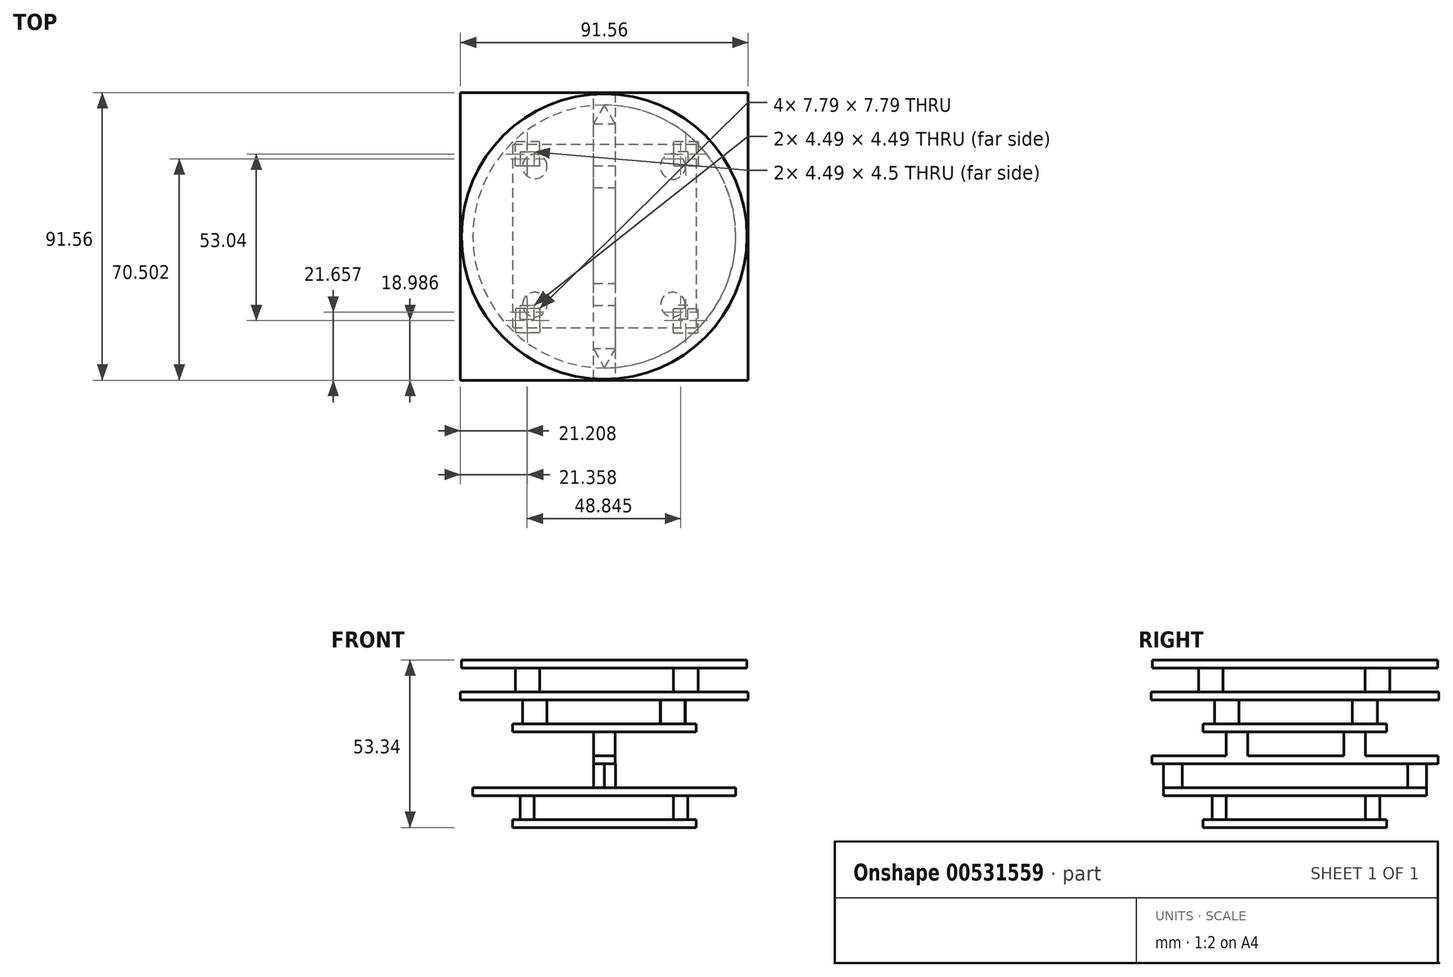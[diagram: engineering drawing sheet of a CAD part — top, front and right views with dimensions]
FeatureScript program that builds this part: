
annotation { "Feature Type Name" : "Feature", "Feature Type Description" : "" }
export const myFeature = defineFeature(function(context is Context, id is Id, definition is map)
    precondition{}
    {
        {
            var Q0;
            Q0=qCreatedBy(makeId("Top.planeOp"),FACE);
            var sketch = newSketch(context, id + "F0", { "sketchPlane" : qUnion([Q0])});
            skLineSegment(sketch, "E0.bottom", {"start": v(29.2, 29.21) * mm, "end": v(-29.21, 29.21) * mm});
            skLineSegment(sketch, "E0.top", {"start": v(29.21, -29.21) * mm, "end": v(-29.2, -29.21) * mm});
            skLineSegment(sketch, "E0.left", {"start": v(29.2, 29.21) * mm, "end": v(29.21, -29.21) * mm});
            skLineSegment(sketch, "E0.right", {"start": v(-29.21, 29.21) * mm, "end": v(-29.2, -29.21) * mm});
            skPoint(sketch, "E0.middle", {"position": v(0, 0) * mm});
            skSolve(sketch);
        }
        {
            var Q0;
            Q0 = qSketchRegion(id + "F0", true);
            extrude(context, id + "F1", {"entities" : qUnion([Q0]), "depth" : 2.54 * mm, "offsetDistance" : 25.4 * mm});
        }
        {
            var Q0;
            Q0=makeQuery(id+"F1.opExtrude","CAP_FACE",FACE,{"disambiguationData":[OSD([sQuery(id+"F0.wireOp",EDGE,"E0.bottom"),sQuery(id+"F0.wireOp",EDGE,"E0.top"),sQuery(id+"F0.wireOp",EDGE,"E0.left"),sQuery(id+"F0.wireOp",EDGE,"E0.right")])],"isStart":false});
            var sketch = newSketch(context, id + "F2", { "sketchPlane" : qUnion([Q0])});
            skLineSegment(sketch, "E1.bottom", {"start": v(-26.82, 26.97) * mm, "end": v(-22.32, 26.97) * mm});
            skLineSegment(sketch, "E1.top", {"start": v(-26.82, 22.47) * mm, "end": v(-22.32, 22.47) * mm});
            skLineSegment(sketch, "E1.left", {"start": v(-26.82, 26.97) * mm, "end": v(-26.82, 22.47) * mm});
            skLineSegment(sketch, "E1.right", {"start": v(-22.32, 26.97) * mm, "end": v(-22.32, 22.47) * mm});
            skSolve(sketch);
        }
        {
            var Q0;
            Q0 = qSketchRegion(id + "F2", true);
            extrude(context, id + "F3", {"entities" : qUnion([Q0]), "operationType" : NewBodyOperationType.ADD, "depth" : 7.62 * mm, "offsetDistance" : 25.4 * mm});
        }
        {
            var Q0;
            Q0=makeQuery(id+"F1.opExtrude","CAP_FACE",FACE,{"disambiguationData":[OSD([sQuery(id+"F0.wireOp",EDGE,"E0.bottom"),sQuery(id+"F0.wireOp",EDGE,"E0.top"),sQuery(id+"F0.wireOp",EDGE,"E0.left"),sQuery(id+"F0.wireOp",EDGE,"E0.right")])],"isStart":false});
            var sketch = newSketch(context, id + "F4", { "sketchPlane" : qUnion([Q0])});
            skLineSegment(sketch, "E2.bottom", {"start": v(26.52, 26.97) * mm, "end": v(22.03, 26.97) * mm});
            skLineSegment(sketch, "E2.top", {"start": v(26.52, 22.47) * mm, "end": v(22.03, 22.47) * mm});
            skLineSegment(sketch, "E2.left", {"start": v(26.52, 26.97) * mm, "end": v(26.52, 22.47) * mm});
            skLineSegment(sketch, "E2.right", {"start": v(22.03, 26.97) * mm, "end": v(22.03, 22.47) * mm});
            skSolve(sketch);
        }
        {
            var Q0;
            Q0 = qSketchRegion(id + "F4", true);
            extrude(context, id + "F5", {"entities" : qUnion([Q0]), "operationType" : NewBodyOperationType.ADD, "depth" : 7.62 * mm, "offsetDistance" : 25.4 * mm});
        }
        {
            var Q0;
            Q0=makeQuery(id+"F1.opExtrude","CAP_FACE",FACE,{"disambiguationData":[OSD([sQuery(id+"F0.wireOp",EDGE,"E0.bottom"),sQuery(id+"F0.wireOp",EDGE,"E0.top"),sQuery(id+"F0.wireOp",EDGE,"E0.left"),sQuery(id+"F0.wireOp",EDGE,"E0.right")])],"isStart":false});
            var sketch = newSketch(context, id + "F6", { "sketchPlane" : qUnion([Q0])});
            skLineSegment(sketch, "E3.bottom", {"start": v(-26.82, -26.37) * mm, "end": v(-22.32, -26.37) * mm});
            skLineSegment(sketch, "E3.top", {"start": v(-26.82, -21.88) * mm, "end": v(-22.32, -21.88) * mm});
            skLineSegment(sketch, "E3.left", {"start": v(-26.82, -26.37) * mm, "end": v(-26.82, -21.88) * mm});
            skLineSegment(sketch, "E3.right", {"start": v(-22.32, -26.37) * mm, "end": v(-22.32, -21.88) * mm});
            skSolve(sketch);
        }
        {
            var Q0;
            Q0 = qSketchRegion(id + "F6", true);
            extrude(context, id + "F7", {"entities" : qUnion([Q0]), "operationType" : NewBodyOperationType.ADD, "depth" : 7.62 * mm, "offsetDistance" : 25.4 * mm});
        }
        {
            var Q0;
            Q0=makeQuery(id+"F1.opExtrude","CAP_FACE",FACE,{"disambiguationData":[OSD([sQuery(id+"F0.wireOp",EDGE,"E0.bottom"),sQuery(id+"F0.wireOp",EDGE,"E0.top"),sQuery(id+"F0.wireOp",EDGE,"E0.left"),sQuery(id+"F0.wireOp",EDGE,"E0.right")])],"isStart":false});
            var sketch = newSketch(context, id + "F8", { "sketchPlane" : qUnion([Q0])});
            skLineSegment(sketch, "E4.bottom", {"start": v(26.52, -26.37) * mm, "end": v(22.03, -26.37) * mm});
            skLineSegment(sketch, "E4.top", {"start": v(26.52, -21.88) * mm, "end": v(22.03, -21.88) * mm});
            skLineSegment(sketch, "E4.left", {"start": v(26.52, -26.37) * mm, "end": v(26.52, -21.88) * mm});
            skLineSegment(sketch, "E4.right", {"start": v(22.03, -26.37) * mm, "end": v(22.03, -21.88) * mm});
            skSolve(sketch);
        }
        {
            var Q0;
            Q0 = qSketchRegion(id + "F8", true);
            extrude(context, id + "F9", {"entities" : qUnion([Q0]), "operationType" : NewBodyOperationType.ADD, "depth" : 7.62 * mm, "offsetDistance" : 25.4 * mm});
        }
        {
            var Q0;
            Q0=makeQuery(id+"F3.opExtrude","CAP_FACE",FACE,{"disambiguationData":[OSD([sQuery(id+"F2.wireOp",EDGE,"E1.bottom"),sQuery(id+"F2.wireOp",EDGE,"E1.top"),sQuery(id+"F2.wireOp",EDGE,"E1.left"),sQuery(id+"F2.wireOp",EDGE,"E1.right")])],"isStart":false});
            var sketch = newSketch(context, id + "F10", { "sketchPlane" : qUnion([Q0])});
            skCircle(sketch, "E5", {"center": v(0, 0) * mm, "radius": 41.85 * mm});
            skSolve(sketch);
        }
        {
            var Q0;
            Q0 = qSketchRegion(id + "F10", true);
            extrude(context, id + "F11", {"entities" : qUnion([Q0]), "operationType" : NewBodyOperationType.ADD, "depth" : 2.54 * mm, "offsetDistance" : 25.4 * mm});
        }
        {
            var Q0;
            Q0=makeQuery(id+"F11.opExtrude","CAP_FACE",FACE,{"disambiguationData":[OSD([sQuery(id+"F10.wireOp",EDGE,"E5")])],"isStart":false});
            var sketch = newSketch(context, id + "F12", { "sketchPlane" : qUnion([Q0])});
            skLineSegment(sketch, "E6", {"start": v(0, 41.85) * mm, "end": v(-3.46, 35.87) * mm});
            skLineSegment(sketch, "E7", {"start": v(-3.46, 35.87) * mm, "end": v(3.45, 35.87) * mm});
            skLineSegment(sketch, "E8", {"start": v(3.45, 35.87) * mm, "end": v(0, 41.85) * mm});
            skSolve(sketch);
        }
        {
            var Q0;
            Q0 = qSketchRegion(id + "F12", true);
            extrude(context, id + "F13", {"entities" : qUnion([Q0]), "operationType" : NewBodyOperationType.ADD, "depth" : 7.62 * mm, "offsetDistance" : 25.4 * mm});
        }
        {
            var Q0;
            Q0=makeQuery(id+"F11.opExtrude","CAP_FACE",FACE,{"disambiguationData":[OSD([sQuery(id+"F10.wireOp",EDGE,"E5")])],"isStart":false});
            var sketch = newSketch(context, id + "F14", { "sketchPlane" : qUnion([Q0])});
            skLineSegment(sketch, "E9", {"start": v(0, -41.85) * mm, "end": v(3.53, -35.83) * mm});
            skLineSegment(sketch, "E10", {"start": v(3.53, -35.83) * mm, "end": v(-3.38, -35.83) * mm});
            skLineSegment(sketch, "E11", {"start": v(-3.38, -35.83) * mm, "end": v(0, -41.85) * mm});
            skSolve(sketch);
        }
        {
            var Q0;
            Q0 = qSketchRegion(id + "F14", true);
            extrude(context, id + "F15", {"entities" : qUnion([Q0]), "operationType" : NewBodyOperationType.ADD, "depth" : 7.62 * mm, "offsetDistance" : 25.4 * mm});
        }
        {
            var Q0;
            Q0=makeQuery(id+"F13.opExtrude","CAP_FACE",FACE,{"disambiguationData":[OSD([sQuery(id+"F12.wireOp",EDGE,"E6"),sQuery(id+"F12.wireOp",EDGE,"E7"),sQuery(id+"F12.wireOp",EDGE,"E8")])],"isStart":false});
            var sketch = newSketch(context, id + "F16", { "sketchPlane" : qUnion([Q0])});
            skLineSegment(sketch, "E12", {"start": v(-3.46, 45.55) * mm, "end": v(3.45, 45.55) * mm});
            skLineSegment(sketch, "E13", {"start": v(3.45, 45.55) * mm, "end": v(3.45, -45.55) * mm});
            skLineSegment(sketch, "E14", {"start": v(3.45, -45.55) * mm, "end": v(-3.46, -45.55) * mm});
            skLineSegment(sketch, "E15", {"start": v(-3.46, -45.55) * mm, "end": v(-3.46, 45.55) * mm});
            skSolve(sketch);
        }
        {
            var Q0;
            Q0 = qSketchRegion(id + "F16", true);
            extrude(context, id + "F17", {"entities" : qUnion([Q0]), "operationType" : NewBodyOperationType.ADD, "depth" : 2.54 * mm, "offsetDistance" : 25.4 * mm});
        }
        {
            var Q0;
            Q0=makeQuery(id+"F17.opExtrude","CAP_FACE",FACE,{"disambiguationData":[OSD([sQuery(id+"F16.wireOp",EDGE,"E12"),sQuery(id+"F16.wireOp",EDGE,"E13"),sQuery(id+"F16.wireOp",EDGE,"E14"),sQuery(id+"F16.wireOp",EDGE,"E15")])],"isStart":false});
            var sketch = newSketch(context, id + "F18", { "sketchPlane" : qUnion([Q0])});
            skLineSegment(sketch, "E16.bottom", {"start": v(-3.46, 22.47) * mm, "end": v(3.45, 22.47) * mm});
            skLineSegment(sketch, "E16.top", {"start": v(-3.46, 15.58) * mm, "end": v(3.45, 15.58) * mm});
            skLineSegment(sketch, "E16.left", {"start": v(-3.46, 22.47) * mm, "end": v(-3.46, 15.58) * mm});
            skLineSegment(sketch, "E16.right", {"start": v(3.45, 22.47) * mm, "end": v(3.45, 15.58) * mm});
            skSolve(sketch);
        }
        {
            var Q0;
            Q0 = qSketchRegion(id + "F18", true);
            extrude(context, id + "F19", {"entities" : qUnion([Q0]), "operationType" : NewBodyOperationType.ADD, "depth" : 7.62 * mm, "offsetDistance" : 25.4 * mm});
        }
        {
            var Q0;
            {var subQ0=sQuery(id+"F16.wireOp",EDGE,"E15");var subQ1=sQuery(id+"F16.wireOp",EDGE,"E14");var subQ2=sQuery(id+"F16.wireOp",EDGE,"E13");Q0=makeQuery(id+"F19.boolean.opBoolean","SPLIT",FACE,{"disambiguationData":[TD([makeQuery(id+"F17.opExtrude","SWEPT_FACE",FACE,{"disambiguationData":[OSD([subQ1])]})])],"derivedFrom":makeQuery(id+"F17.opExtrude","CAP_FACE",FACE,{"disambiguationData":[OSD([sQuery(id+"F16.wireOp",EDGE,"E12"),subQ2,subQ1,subQ0])],"isStart":false})});}
            var sketch = newSketch(context, id + "F20", { "sketchPlane" : qUnion([Q0])});
            skLineSegment(sketch, "E17.bottom", {"start": v(-3.46, -14.98) * mm, "end": v(3.45, -14.98) * mm});
            skLineSegment(sketch, "E17.top", {"start": v(-3.46, -21.88) * mm, "end": v(3.45, -21.88) * mm});
            skLineSegment(sketch, "E17.left", {"start": v(-3.46, -14.98) * mm, "end": v(-3.46, -21.88) * mm});
            skLineSegment(sketch, "E17.right", {"start": v(3.45, -14.98) * mm, "end": v(3.45, -21.88) * mm});
            skSolve(sketch);
        }
        {
            var Q0;
            Q0 = qSketchRegion(id + "F20", true);
            extrude(context, id + "F21", {"entities" : qUnion([Q0]), "operationType" : NewBodyOperationType.ADD, "depth" : 7.62 * mm, "offsetDistance" : 25.4 * mm});
        }
        {
            var Q0;
            Q0=makeQuery(id+"F19.opExtrude","CAP_FACE",FACE,{"disambiguationData":[OSD([sQuery(id+"F18.wireOp",EDGE,"E16.bottom"),sQuery(id+"F18.wireOp",EDGE,"E16.top"),sQuery(id+"F18.wireOp",EDGE,"E16.left"),sQuery(id+"F18.wireOp",EDGE,"E16.right")])],"isStart":false});
            var sketch = newSketch(context, id + "F22", { "sketchPlane" : qUnion([Q0])});
            skLineSegment(sketch, "E18.bottom", {"start": v(29.2, 29.21) * mm, "end": v(-29.21, 29.21) * mm});
            skLineSegment(sketch, "E18.top", {"start": v(29.21, -29.21) * mm, "end": v(-29.2, -29.21) * mm});
            skLineSegment(sketch, "E18.left", {"start": v(29.2, 29.21) * mm, "end": v(29.21, -29.21) * mm});
            skLineSegment(sketch, "E18.right", {"start": v(-29.21, 29.21) * mm, "end": v(-29.2, -29.21) * mm});
            skPoint(sketch, "E18.middle", {"position": v(0, 0) * mm});
            skSolve(sketch);
        }
        {
            var Q0;
            Q0 = qSketchRegion(id + "F22", true);
            extrude(context, id + "F23", {"entities" : qUnion([Q0]), "operationType" : NewBodyOperationType.ADD, "depth" : 2.54 * mm, "offsetDistance" : 25.4 * mm});
        }
        {
            var Q0;
            Q0=makeQuery(id+"F23.opExtrude","CAP_FACE",FACE,{"disambiguationData":[OSD([sQuery(id+"F22.wireOp",EDGE,"E18.bottom"),sQuery(id+"F22.wireOp",EDGE,"E18.top"),sQuery(id+"F22.wireOp",EDGE,"E18.left"),sQuery(id+"F22.wireOp",EDGE,"E18.right")])],"isStart":false});
            var sketch = newSketch(context, id + "F24", { "sketchPlane" : qUnion([Q0])});
            skCircle(sketch, "E19", {"center": v(-22.11, 22.27) * mm, "radius": 3.89 * mm});
            skCircle(sketch, "E20", {"center": v(-22.11, -21.67) * mm, "radius": 3.89 * mm});
            skCircle(sketch, "E21", {"center": v(21.82, -21.67) * mm, "radius": 3.89 * mm});
            skCircle(sketch, "E22", {"center": v(21.82, 22.27) * mm, "radius": 4.03 * mm});
            skSolve(sketch);
        }
        {
            var Q0;
            Q0 = qSketchRegion(id + "F24", true);
            extrude(context, id + "F25", {"entities" : qUnion([Q0]), "operationType" : NewBodyOperationType.ADD, "depth" : 7.62 * mm, "offsetDistance" : 25.4 * mm});
        }
        {
            var Q0;
            Q0=makeQuery(id+"F25.opExtrude","CAP_FACE",FACE,{"disambiguationData":[OSD([sQuery(id+"F24.wireOp",EDGE,"E22")])],"isStart":false});
            var sketch = newSketch(context, id + "F26", { "sketchPlane" : qUnion([Q0])});
            skLineSegment(sketch, "E23.bottom", {"start": v(-45.78, 45.78) * mm, "end": v(45.78, 45.78) * mm});
            skLineSegment(sketch, "E23.top", {"start": v(-45.78, -45.78) * mm, "end": v(45.78, -45.78) * mm});
            skLineSegment(sketch, "E23.left", {"start": v(-45.78, 45.78) * mm, "end": v(-45.78, -45.78) * mm});
            skLineSegment(sketch, "E23.right", {"start": v(45.78, 45.78) * mm, "end": v(45.78, -45.78) * mm});
            skPoint(sketch, "E23.middle", {"position": v(0, 0) * mm});
            skSolve(sketch);
        }
        {
            var Q0;
            Q0 = qSketchRegion(id + "F26", true);
            extrude(context, id + "F27", {"entities" : qUnion([Q0]), "operationType" : NewBodyOperationType.ADD, "depth" : 2.54 * mm, "offsetDistance" : 25.4 * mm});
        }
        {
            var Q0;
            Q0=makeQuery(id+"F27.opExtrude","CAP_FACE",FACE,{"disambiguationData":[OSD([sQuery(id+"F26.wireOp",EDGE,"E23.bottom"),sQuery(id+"F26.wireOp",EDGE,"E23.top"),sQuery(id+"F26.wireOp",EDGE,"E23.left"),sQuery(id+"F26.wireOp",EDGE,"E23.right")])],"isStart":false});
            var sketch = newSketch(context, id + "F28", { "sketchPlane" : qUnion([Q0])});
            skLineSegment(sketch, "E24.bottom", {"start": v(-20.53, 22.35) * mm, "end": v(-28.32, 22.35) * mm});
            skLineSegment(sketch, "E24.top", {"start": v(-20.53, 30.14) * mm, "end": v(-28.32, 30.14) * mm});
            skLineSegment(sketch, "E24.left", {"start": v(-20.53, 22.35) * mm, "end": v(-20.53, 30.14) * mm});
            skLineSegment(sketch, "E24.right", {"start": v(-28.32, 22.35) * mm, "end": v(-28.32, 30.14) * mm});
            skPoint(sketch, "E24.middle", {"position": v(-24.42, 26.25) * mm});
            skLineSegment(sketch, "E25.bottom", {"start": v(29.82, 30.14) * mm, "end": v(22.03, 30.14) * mm});
            skLineSegment(sketch, "E25.top", {"start": v(29.82, 22.35) * mm, "end": v(22.03, 22.35) * mm});
            skLineSegment(sketch, "E25.left", {"start": v(29.82, 30.14) * mm, "end": v(29.82, 22.35) * mm});
            skLineSegment(sketch, "E25.right", {"start": v(22.03, 30.14) * mm, "end": v(22.03, 22.35) * mm});
            skPoint(sketch, "E25.middle", {"position": v(25.92, 26.25) * mm});
            skPoint(sketch, "E25.middle.positionSnap0", {"position": v(-20.53, 26.25) * mm});
            skPoint(sketch, "E25.centerSnap0", {"position": v(-20.53, 26.25) * mm});
            skLineSegment(sketch, "E26.bottom", {"start": v(22.03, -30.69) * mm, "end": v(29.82, -30.69) * mm});
            skLineSegment(sketch, "E26.top", {"start": v(22.03, -22.9) * mm, "end": v(29.82, -22.9) * mm});
            skLineSegment(sketch, "E26.left", {"start": v(22.03, -30.69) * mm, "end": v(22.03, -22.9) * mm});
            skLineSegment(sketch, "E26.right", {"start": v(29.82, -30.69) * mm, "end": v(29.82, -22.9) * mm});
            skPoint(sketch, "E26.middle", {"position": v(25.92, -26.8) * mm});
            skPoint(sketch, "E26.middle.positionSnap0", {"position": v(25.92, 22.35) * mm});
            skPoint(sketch, "E26.centerSnap0", {"position": v(25.92, 22.35) * mm});
            skLineSegment(sketch, "E27.bottom", {"start": v(-20.53, -22.9) * mm, "end": v(-28.32, -22.9) * mm});
            skLineSegment(sketch, "E27.top", {"start": v(-20.53, -30.69) * mm, "end": v(-28.32, -30.69) * mm});
            skLineSegment(sketch, "E27.left", {"start": v(-20.53, -22.9) * mm, "end": v(-20.53, -30.69) * mm});
            skLineSegment(sketch, "E27.right", {"start": v(-28.32, -22.9) * mm, "end": v(-28.32, -30.69) * mm});
            skPoint(sketch, "E27.middle", {"position": v(-24.42, -26.8) * mm});
            skPoint(sketch, "E27.middle.positionSnap0", {"position": v(22.03, -26.8) * mm});
            skPoint(sketch, "E27.centerSnap0", {"position": v(22.03, -26.8) * mm});
            skSolve(sketch);
        }
        {
            var Q0;
            Q0 = qSketchRegion(id + "F28", true);
            extrude(context, id + "F29", {"entities" : qUnion([Q0]), "operationType" : NewBodyOperationType.ADD, "depth" : 7.62 * mm, "offsetDistance" : 25.4 * mm});
        }
        {
            var Q0;
            Q0=makeQuery(id+"F29.opExtrude","CAP_FACE",FACE,{"disambiguationData":[OSD([sQuery(id+"F28.wireOp",EDGE,"E24.bottom"),sQuery(id+"F28.wireOp",EDGE,"E24.top"),sQuery(id+"F28.wireOp",EDGE,"E24.left"),sQuery(id+"F28.wireOp",EDGE,"E24.right")])],"isStart":false});
            var sketch = newSketch(context, id + "F30", { "sketchPlane" : qUnion([Q0])});
            skCircle(sketch, "E28", {"center": v(0, 0) * mm, "radius": 45.42 * mm});
            skSolve(sketch);
        }
        {
            var Q0;
            Q0 = qSketchRegion(id + "F30", true);
            extrude(context, id + "F31", {"entities" : qUnion([Q0]), "operationType" : NewBodyOperationType.ADD, "depth" : 2.54 * mm, "offsetDistance" : 25.4 * mm});
        }
    });
